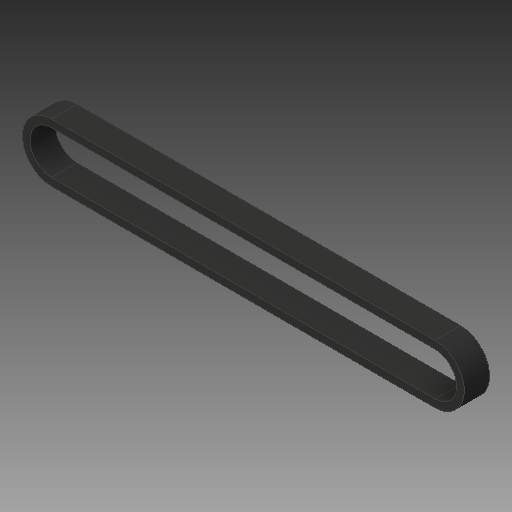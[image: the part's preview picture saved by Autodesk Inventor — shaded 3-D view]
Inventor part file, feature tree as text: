
AUTODESK INVENTOR PART (.ipt)
format: ipt  version: 2019 (Build 230136000, 136)  size: 109,056 bytes
history: native  units: mm
features: extrude x1, sketch x1
ambient origin geometry x8: Origin, YZ Plane, XZ Plane, XY Plane, X Axis, Y Axis, Z Axis, Center Point
bodies: Solid1 (feature_tree)
feature tree (2):
  extrude  "Extrusion1"  Depth=23.0mm
  sketch  "Sketch1"  dims[d0=151.0mm d1=23.0mm d2=3.0mm d3=3.0mm d4=11.5mm d5=8.5mm d7=8.5mm d8=151.0mm d9=151.0mm d10=10.0mm d11=0.0mm]
